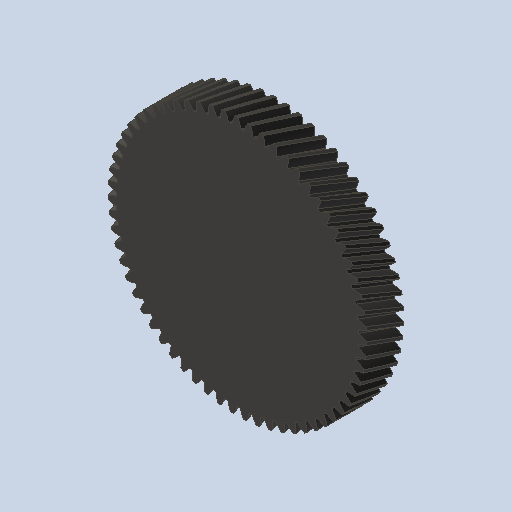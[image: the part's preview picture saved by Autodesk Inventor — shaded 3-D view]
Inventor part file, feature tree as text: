
AUTODESK INVENTOR PART (.ipt)
format: ipt  version: 2023 (Build 270158000, 158)  size: 827,904 bytes
history: native  units: mm (DEFAULTED — no unit token found)
features: plane x3, other x3, sketch x2, extrude x1
ambient origin geometry x8: Origin, YZ Plane, XZ Plane, XY Plane, X Axis, Y Axis, Z Axis, Center Point
bodies: Solid1 (feature_tree)
feature tree (9):
  extrude  "Extrusion1"  Depth=15.0mm TaperAngle=0.0deg
  plane  "Work Plane2"
  plane  "Work Plane8"
  plane  "Work Plane9"
  other  "Spur Gear"
  sketch  "Sketch1"  dims[d0=104.529867mm d1=15.0mm d2=0.0mm]
  sketch  "Sketch2"  dims[d3=100.5648mm d4=10.0mm d5=0.0mm d16=57.15mm d17=0.0mm d34=0.498666mm d39=0.0mm d41=0.0mm d43=57.15mm d46=57.15mm d47=0.0mm d48=0.0mm]
  other  "Srf1"
  other  "Pitch Diameter"
